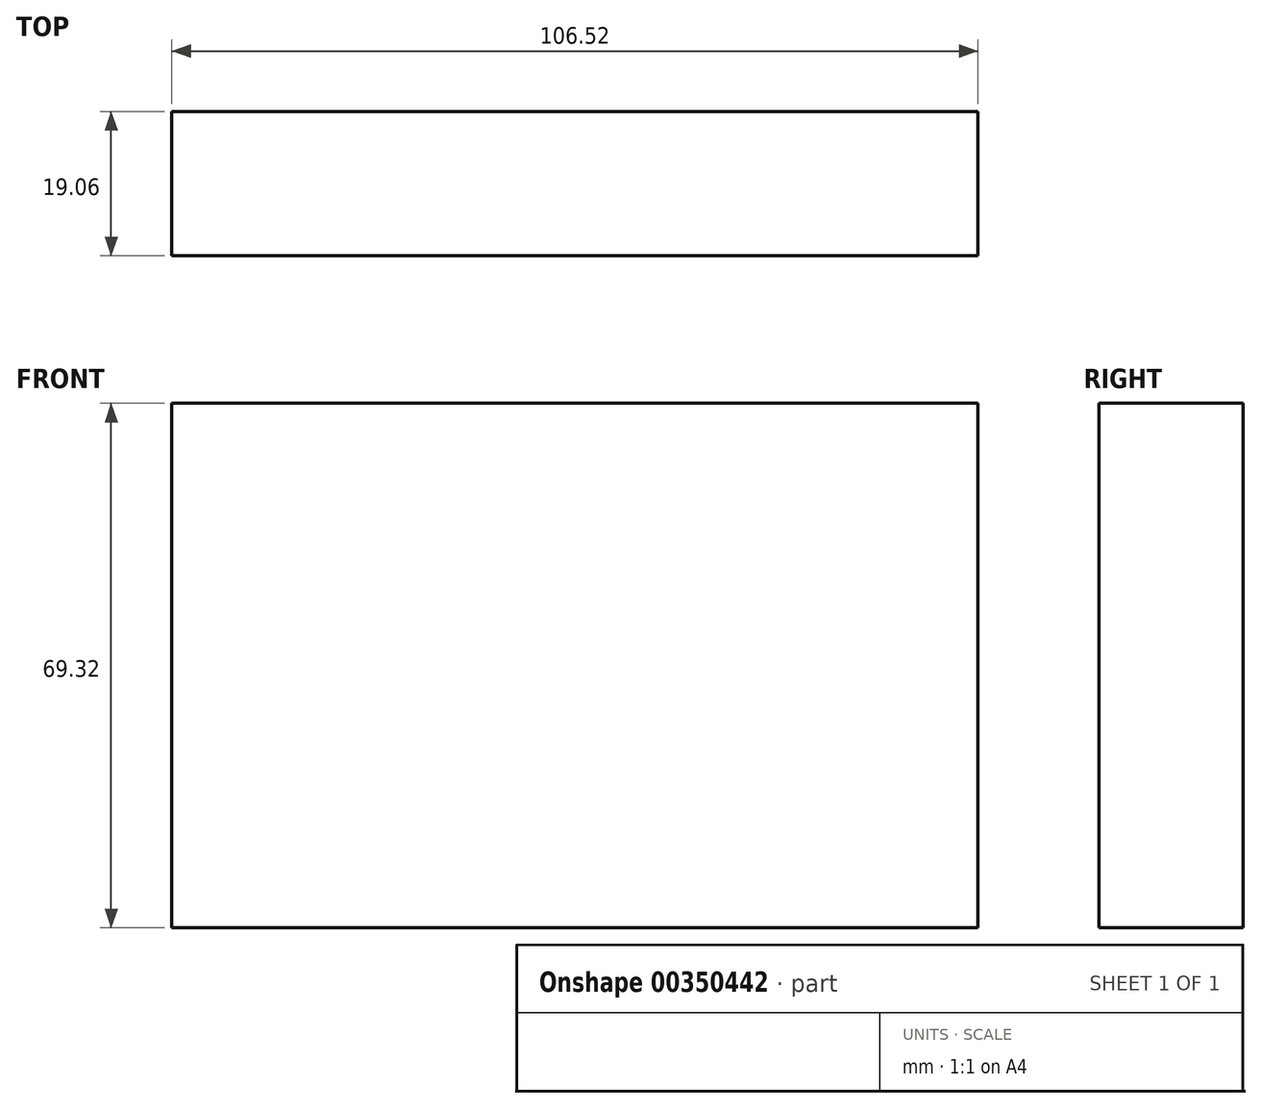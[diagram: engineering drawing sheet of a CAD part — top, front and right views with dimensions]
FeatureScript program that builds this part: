
annotation { "Feature Type Name" : "Feature", "Feature Type Description" : "" }
export const myFeature = defineFeature(function(context is Context, id is Id, definition is map)
    precondition{}
    {
        {
            var Q0;
            Q0=qCreatedBy(makeId("Front.planeOp"),FACE);
            var sketch = newSketch(context, id + "F0", { "sketchPlane" : qUnion([Q0])});
            skLineSegment(sketch, "E0.bottom", {"start": v(-53.26, 34.66) * mm, "end": v(53.26, 34.66) * mm});
            skLineSegment(sketch, "E0.top", {"start": v(-53.26, -34.66) * mm, "end": v(53.26, -34.66) * mm});
            skLineSegment(sketch, "E0.left", {"start": v(-53.26, 34.66) * mm, "end": v(-53.26, -34.66) * mm});
            skLineSegment(sketch, "E0.right", {"start": v(53.26, 34.66) * mm, "end": v(53.26, -34.66) * mm});
            skPoint(sketch, "E0.middle", {"position": v(0, 0) * mm});
            skSolve(sketch);
        }
        {
            var Q0;
            Q0=makeQuery(id+"F0.imprint","IMPRINT",FACE,{"disambiguationData":[TD([[makeQuery(id+"F0.imprint","IMPRINT",EDGE,{"derivedFrom":sQuery(id+"F0.wireOp",EDGE,"E0.bottom")}),-1.0]])]});
            extrude(context, id + "F1", {"entities" : qUnion([Q0]), "endBound" : BoundingType.SYMMETRIC, "depth" : 19.05 * mm});
        }
    });
